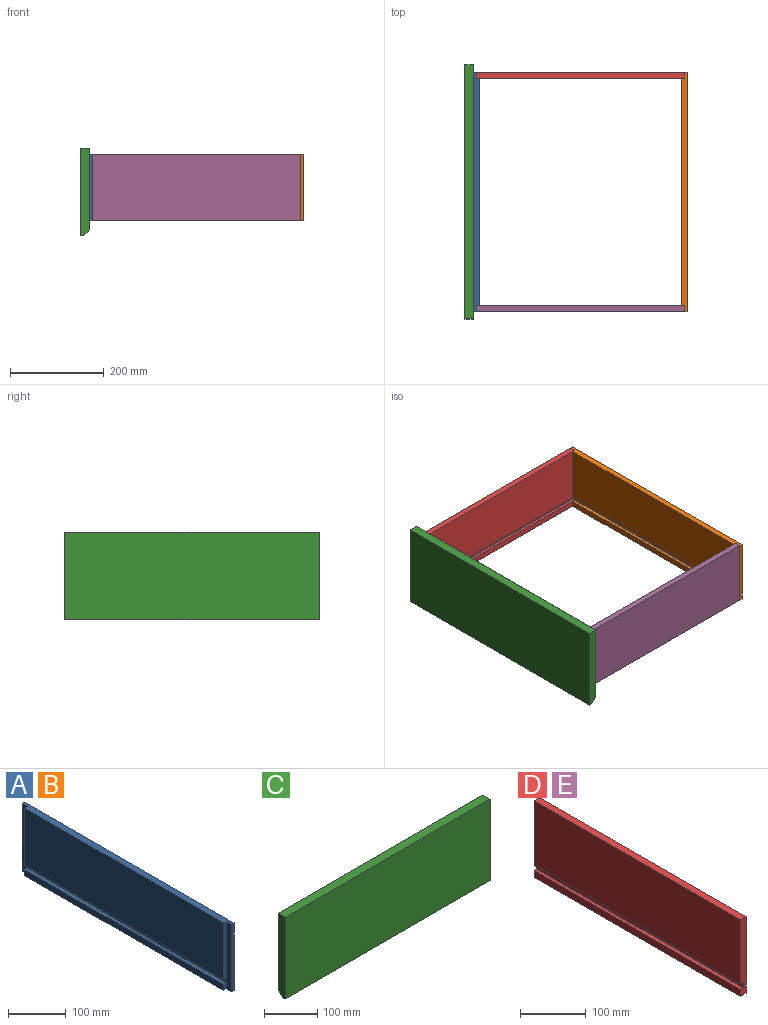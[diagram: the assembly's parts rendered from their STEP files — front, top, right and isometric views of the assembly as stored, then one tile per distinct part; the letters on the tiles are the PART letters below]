
ASSEMBLY  parts=5 mates=4
PART A: 14 faces, bbox 12.7x511.2x142.9 mm
  f0: plane 485.78x12.7mm, normal (-1,0,0), area 6169.3mm2, adj f6,f9,f10,f12
  f1: plane 120.65x6.35mm, normal (0,-1,0), area 766.1mm2, adj f3,f4,f11,f13
  f2: plane 120.65x6.35mm, normal (0,1,0), area 766.1mm2, adj f3,f4,f11,f13
  f3: plane 511.18x12.7mm, normal (0,0,1), area 6330.6mm2, adj f1,f2,f4,f5,f7,f8,f11
  f4: plane 485.78x120.65mm, normal (-1,0,0), area 58608.8mm2, adj f1,f2,f3,f13
  f5: plane 142.88x6.35mm, normal (0,-1,0), area 907.3mm2, adj f3,f6,f8,f11
  f6: plane 511.18x12.7mm, normal (0,0,-1), area 6330.6mm2, adj f0,f5,f7,f8,f9,f10,f11
  f7: plane 142.88x6.35mm, normal (0,1,0), area 907.3mm2, adj f3,f6,f8,f11
  f8: plane 511.18x142.88mm, normal (1,0,0), area 73034.1mm2, adj f3,f5,f6,f7
  f9: plane 12.7x6.35mm, normal (0,-1,0), area 80.6mm2, adj f0,f6,f11,f12
  f10: plane 12.7x6.35mm, normal (0,1,0), area 80.6mm2, adj f0,f6,f11,f12
  f11: plane 511.18x142.88mm, normal (-1,0,0), area 8256mm2, adj f1,f2,f3,f5,f6,f7,f9,f10
  f12: plane 485.78x6.35mm, normal (0,0,1), area 3084.7mm2, adj f0,f9,f10,f11
  f13: plane 485.78x6.35mm, normal (0,0,-1), area 3084.7mm2, adj f1,f2,f4,f11
PART B: same geometry as A
PART C: 7 faces, bbox 542.9x19.1x187.3 mm
  f0: plane 187.33x19.05mm, normal (-1,0,0), area 3487.9mm2, adj f1,f3,f4,f5,f6
  f1: plane 542.93x6.35mm, normal (0,0,-1), area 3447.6mm2, adj f0,f2,f4,f6
  f2: plane 187.33x19.05mm, normal (1,0,0), area 3487.9mm2, adj f1,f3,f4,f5,f6
  f3: plane 542.93x19.05mm, normal (0,0,1), area 10342.7mm2, adj f0,f2,f4,f5
  f4: plane 542.93x187.33mm, normal (0,-1,0), area 101703.4mm2, adj f0,f1,f2,f3
  f5: plane 542.93x174.63mm, normal (0,1,0), area 94808.3mm2, adj f0,f2,f3,f6
  f6: plane 542.93x12.7mm, normal (0,0.71,-0.71), area 9751.2mm2, adj f0,f1,f2,f5
PART D: 10 faces, bbox 12.7x444.5x142.9 mm
  f0: plane 444.5x12.7mm, normal (-1,0,0), area 5645.2mm2, adj f1,f2,f3,f8
  f1: plane 142.88x12.7mm, normal (0,-1,0), area 1754mm2, adj f0,f2,f4,f5,f6,f7,f8,f9
  f2: plane 444.5x12.7mm, normal (0,0,-1), area 5645.2mm2, adj f0,f1,f3,f5
  f3: plane 142.88x12.7mm, normal (0,1,0), area 1754mm2, adj f0,f2,f4,f5,f6,f7,f8,f9
  f4: plane 444.5x12.7mm, normal (0,0,1), area 5645.2mm2, adj f1,f3,f5,f6
  f5: plane 444.5x142.88mm, normal (1,0,0), area 63507.9mm2, adj f1,f2,f3,f4
  f6: plane 444.5x120.65mm, normal (-1,0,0), area 53628.9mm2, adj f1,f3,f4,f7
  f7: plane 444.5x6.35mm, normal (0,0,-1), area 2822.6mm2, adj f1,f3,f6,f9
  f8: plane 444.5x6.35mm, normal (0,0,1), area 2822.6mm2, adj f0,f1,f3,f9
  f9: plane 444.5x9.53mm, normal (-1,0,0), area 4233.9mm2, adj f1,f3,f7,f8
PART E: same geometry as D
PLACE A rot(axis=(0,0,-1),180deg) t=(-241.4,257.51,182.53)mm
PLACE B t=(190.4,-253.67,182.53)mm
PLACE C rot(axis=(0,0,-1),90deg) t=(-254.1,273.38,150.78)mm
PLACE D rot(axis=(0,0,1),90deg) t=(196.75,244.81,182.53)mm
PLACE E rot(axis=(0,0,-1),90deg) t=(-247.75,-240.97,182.53)mm
MATE fastened B.f11 <-> D.f1  axis (-1,0,0) through (196.75,257.51,325.41)mm
MATE fastened A.f11 <-> D.f3  axis (1,0,0) through (-247.75,257.51,325.41)mm
MATE fastened E.f3 <-> B.f11  axis (1,0,0) through (196.75,-253.67,325.41)mm
MATE fastened A.f8 <-> C.f5  axis (-1,0,0) through (-254.1,1.92,325.41)mm
